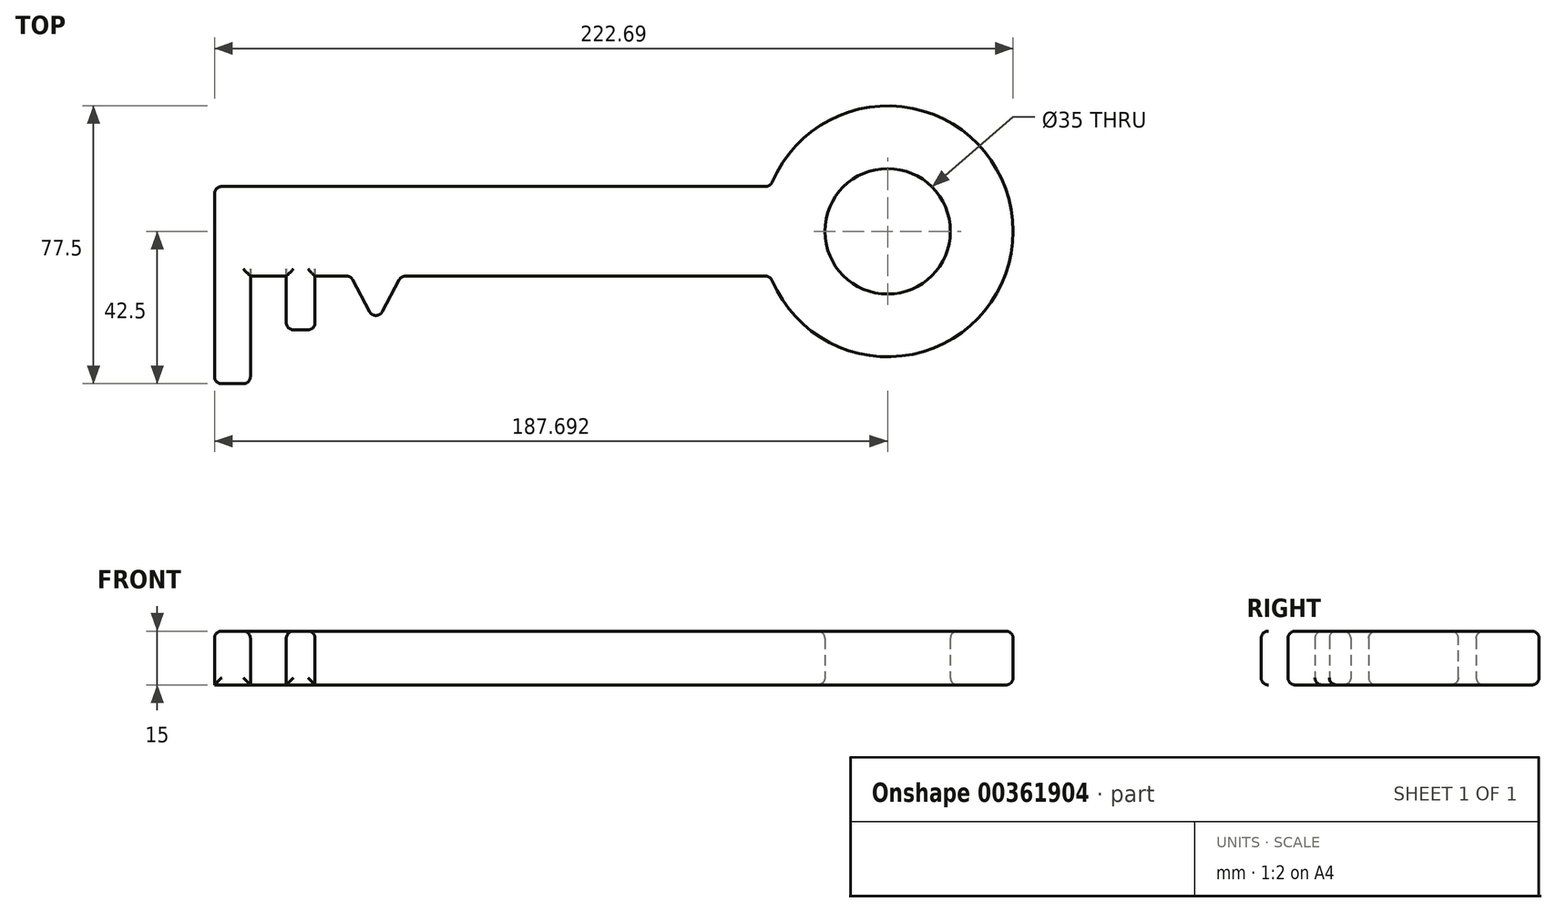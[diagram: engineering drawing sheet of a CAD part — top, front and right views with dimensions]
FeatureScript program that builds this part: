
annotation { "Feature Type Name" : "Feature", "Feature Type Description" : "" }
export const myFeature = defineFeature(function(context is Context, id is Id, definition is map)
    precondition{}
    {
        {
            var Q0;
            Q0=qCreatedBy(makeId("Top.planeOp"),FACE);
            var sketch = newSketch(context, id + "F0", { "sketchPlane" : qUnion([Q0])});
            skLineSegment(sketch, "E0.bottom", {"start": v(0, 0) * mm, "end": v(-155, 0) * mm});
            skLineSegment(sketch, "E0.top", {"start": v(0, 25) * mm, "end": v(-155, 25) * mm});
            skLineSegment(sketch, "E0.left", {"start": v(0, 0) * mm, "end": v(0, 25) * mm});
            skLineSegment(sketch, "E0.right", {"start": v(-155, 0) * mm, "end": v(-155, 25) * mm});
            skLineSegment(sketch, "E1.bottom", {"start": v(-155, 0) * mm, "end": v(-145, 0) * mm});
            skLineSegment(sketch, "E1.top", {"start": v(-155, -30) * mm, "end": v(-145, -30) * mm});
            skLineSegment(sketch, "E1.left", {"start": v(-155, 0) * mm, "end": v(-155, -30) * mm});
            skLineSegment(sketch, "E1.right", {"start": v(-145, 0) * mm, "end": v(-145, -30) * mm});
            skLineSegment(sketch, "E2.bottom", {"start": v(-135, 0) * mm, "end": v(-127, 0) * mm});
            skLineSegment(sketch, "E2.top", {"start": v(-135, -15) * mm, "end": v(-127, -15) * mm});
            skLineSegment(sketch, "E2.left", {"start": v(-135, 0) * mm, "end": v(-135, -15) * mm});
            skLineSegment(sketch, "E2.right", {"start": v(-127, 0) * mm, "end": v(-127, -15) * mm});
            skLineSegment(sketch, "E3", {"start": v(-117, 0) * mm, "end": v(-110, -13.26) * mm});
            skLineSegment(sketch, "E4", {"start": v(-110, 0) * mm, "end": v(-110, -13.26) * mm});
            skLineSegment(sketch, "E5", {"start": v(-110, -13.26) * mm, "end": v(-102.98, 0) * mm});
            skArc(sketch, "E6", {"start": v(0, 0) * mm, "mid": v(67.7, 12.5) * mm, "end": v(0, 25) * mm});
            skCircle(sketch, "E7", {"center": v(32.7, 12.5) * mm, "radius": 17.5 * mm});
            skLineSegment(sketch, "E8", {"start": v(32.7, 12.5) * mm, "end": v(-155, 12.5) * mm, "construction": true});
            skSolve(sketch);
        }
        {
            var Q0;
            Q0 = qSketchRegion(id + "F0", true);
            extrude(context, id + "F1", {"entities" : qUnion([Q0]), "depth" : 15 * mm});
        }
        {
            var Q0;
            Q0=makeQuery(id+"F1.opExtrude","CAP_EDGE",EDGE,{"disambiguationData":[OSD([sQuery(id+"F0.wireOp",EDGE,"E0.top")])],"isStart":false});
            var Q1;
            {var subQ0=sQuery(id+"F0.wireOp",EDGE,"E0.bottom");Q1=makeQuery(id+"F1.opExtrude","CAP_EDGE",EDGE,{"disambiguationData":[OSD([subQ0]),TDD([makeQuery(id+"F0.imprint","IMPRINT",EDGE,{"disambiguationData":[TD([[makeQuery(id+"F0.imprint","INTERSECT",VERTEX,{"derivedFrom":[subQ0,sQuery(id+"F0.wireOp",EDGE,"E5")]}),1.0]])],"derivedFrom":subQ0})])],"isStart":true});}
            var Q2;
            Q2=makeQuery(id+"F1.opExtrude","CAP_EDGE",EDGE,{"disambiguationData":[OSD([sQuery(id+"F0.wireOp",EDGE,"E0.right"),sQuery(id+"F0.wireOp",EDGE,"E1.left")])],"isStart":false});
            var Q3;
            Q3=makeQuery(id+"F1.opExtrude","CAP_EDGE",EDGE,{"disambiguationData":[OSD([sQuery(id+"F0.wireOp",EDGE,"E1.top")])],"isStart":false});
            var Q4;
            Q4=makeQuery(id+"F1.opExtrude","CAP_EDGE",EDGE,{"disambiguationData":[OSD([sQuery(id+"F0.wireOp",EDGE,"E1.right")])],"isStart":false});
            var Q5;
            {var subQ0=sQuery(id+"F0.wireOp",EDGE,"E0.bottom");Q5=makeQuery(id+"F1.opExtrude","CAP_EDGE",EDGE,{"disambiguationData":[OSD([subQ0]),TDD([makeQuery(id+"F0.imprint","IMPRINT",EDGE,{"disambiguationData":[TD([[makeQuery(id+"F0.imprint","INTERSECT",VERTEX,{"derivedFrom":[subQ0,sQuery(id+"F0.wireOp",EDGE,"E1.bottom"),sQuery(id+"F0.wireOp",EDGE,"E1.right")]}),1.0]])],"derivedFrom":subQ0})])],"isStart":false});}
            var Q6;
            Q6=makeQuery(id+"F1.opExtrude","CAP_EDGE",EDGE,{"disambiguationData":[OSD([sQuery(id+"F0.wireOp",EDGE,"E2.left")])],"isStart":false});
            var Q7;
            Q7=makeQuery(id+"F1.opExtrude","CAP_EDGE",EDGE,{"disambiguationData":[OSD([sQuery(id+"F0.wireOp",EDGE,"E2.top")])],"isStart":false});
            var Q8;
            {var subQ0=sQuery(id+"F0.wireOp",EDGE,"E0.bottom");Q8=makeQuery(id+"F1.opExtrude","CAP_EDGE",EDGE,{"disambiguationData":[OSD([subQ0]),TDD([makeQuery(id+"F0.imprint","IMPRINT",EDGE,{"disambiguationData":[TD([[makeQuery(id+"F0.imprint","INTERSECT",VERTEX,{"derivedFrom":[subQ0,sQuery(id+"F0.wireOp",EDGE,"E3")]}),-1.0]])],"derivedFrom":subQ0})])],"isStart":true});}
            var Q9;
            Q9=makeQuery(id+"F1.opExtrude","CAP_EDGE",EDGE,{"disambiguationData":[OSD([sQuery(id+"F0.wireOp",EDGE,"E3")])],"isStart":false});
            var Q10;
            Q10=makeQuery(id+"F1.opExtrude","CAP_EDGE",EDGE,{"disambiguationData":[OSD([sQuery(id+"F0.wireOp",EDGE,"E5")])],"isStart":true});
            var Q11;
            Q11=makeQuery(id+"F1.opExtrude","CAP_EDGE",EDGE,{"disambiguationData":[OSD([sQuery(id+"F0.wireOp",EDGE,"E6")])],"isStart":false});
            var Q12;
            Q12=makeQuery(id+"F1.opExtrude","CAP_EDGE",EDGE,{"disambiguationData":[OSD([sQuery(id+"F0.wireOp",EDGE,"E7")])],"isStart":true});
            var Q13;
            Q13=makeQuery(id+"F1.opExtrude","CAP_EDGE",EDGE,{"disambiguationData":[OSD([sQuery(id+"F0.wireOp",EDGE,"E0.top")])],"isStart":true});
            var Q14;
            Q14=makeQuery(id+"F1.opExtrude","SWEPT_FACE",FACE,{"disambiguationData":[OSD([sQuery(id+"F0.wireOp",EDGE,"E6")])]});
            var Q15;
            Q15=makeQuery(id+"F1.opExtrude","CAP_EDGE",EDGE,{"disambiguationData":[OSD([sQuery(id+"F0.wireOp",EDGE,"E6")])],"isStart":true});
            var Q16;
            {var subQ0=sQuery(id+"F0.wireOp",EDGE,"E0.bottom");Q16=makeQuery(id+"F1.opExtrude","CAP_EDGE",EDGE,{"disambiguationData":[OSD([subQ0]),TDD([makeQuery(id+"F0.imprint","IMPRINT",EDGE,{"disambiguationData":[TD([[makeQuery(id+"F0.imprint","INTERSECT",VERTEX,{"derivedFrom":[subQ0,sQuery(id+"F0.wireOp",EDGE,"E5")]}),1.0]])],"derivedFrom":subQ0})])],"isStart":false});}
            var Q17;
            Q17=makeQuery(id+"F1.opExtrude","SWEPT_EDGE",EDGE,{"disambiguationData":[OSD([sQuery(id+"F0.wireOp",EDGE,"E0.bottom"),sQuery(id+"F0.wireOp",EDGE,"E5")])]});
            var Q18;
            Q18=makeQuery(id+"F1.opExtrude","SWEPT_EDGE",EDGE,{"disambiguationData":[OSD([sQuery(id+"F0.wireOp",EDGE,"E3"),sQuery(id+"F0.wireOp",EDGE,"E4"),sQuery(id+"F0.wireOp",EDGE,"E5")])]});
            var Q19;
            Q19=makeQuery(id+"F1.opExtrude","CAP_EDGE",EDGE,{"disambiguationData":[OSD([sQuery(id+"F0.wireOp",EDGE,"E5")])],"isStart":false});
            var Q20;
            Q20=makeQuery(id+"F1.opExtrude","CAP_EDGE",EDGE,{"disambiguationData":[OSD([sQuery(id+"F0.wireOp",EDGE,"E3")])],"isStart":true});
            var Q21;
            Q21=makeQuery(id+"F1.opExtrude","SWEPT_EDGE",EDGE,{"disambiguationData":[OSD([sQuery(id+"F0.wireOp",EDGE,"E0.bottom"),sQuery(id+"F0.wireOp",EDGE,"E3")])]});
            var Q22;
            {var subQ0=sQuery(id+"F0.wireOp",EDGE,"E0.bottom");Q22=makeQuery(id+"F1.opExtrude","CAP_EDGE",EDGE,{"disambiguationData":[OSD([subQ0]),TDD([makeQuery(id+"F0.imprint","IMPRINT",EDGE,{"disambiguationData":[TD([[makeQuery(id+"F0.imprint","INTERSECT",VERTEX,{"derivedFrom":[subQ0,sQuery(id+"F0.wireOp",EDGE,"E3")]}),-1.0]])],"derivedFrom":subQ0})])],"isStart":false});}
            var Q23;
            Q23=makeQuery(id+"F1.opExtrude","CAP_EDGE",EDGE,{"disambiguationData":[OSD([sQuery(id+"F0.wireOp",EDGE,"E2.right")])],"isStart":false});
            var Q24;
            Q24=makeQuery(id+"F1.opExtrude","CAP_EDGE",EDGE,{"disambiguationData":[OSD([sQuery(id+"F0.wireOp",EDGE,"E2.top")])],"isStart":true});
            var Q25;
            {var subQ0=sQuery(id+"F0.wireOp",EDGE,"E0.bottom");Q25=makeQuery(id+"F1.opExtrude","CAP_EDGE",EDGE,{"disambiguationData":[OSD([subQ0]),TDD([makeQuery(id+"F0.imprint","IMPRINT",EDGE,{"disambiguationData":[TD([[makeQuery(id+"F0.imprint","INTERSECT",VERTEX,{"derivedFrom":[subQ0,sQuery(id+"F0.wireOp",EDGE,"E1.bottom"),sQuery(id+"F0.wireOp",EDGE,"E1.right")]}),1.0]])],"derivedFrom":subQ0})])],"isStart":true});}
            var Q26;
            Q26=makeQuery(id+"F1.opExtrude","SWEPT_EDGE",EDGE,{"disambiguationData":[OSD([sQuery(id+"F0.wireOp",EDGE,"E2.top"),sQuery(id+"F0.wireOp",EDGE,"E2.left")])]});
            var Q27;
            Q27=makeQuery(id+"F1.opExtrude","SWEPT_EDGE",EDGE,{"disambiguationData":[OSD([sQuery(id+"F0.wireOp",EDGE,"E1.top"),sQuery(id+"F0.wireOp",EDGE,"E1.right")])]});
            var Q28;
            Q28=makeQuery(id+"F1.opExtrude","CAP_EDGE",EDGE,{"disambiguationData":[OSD([sQuery(id+"F0.wireOp",EDGE,"E1.top")])],"isStart":true});
            var Q29;
            Q29=makeQuery(id+"F1.opExtrude","SWEPT_EDGE",EDGE,{"disambiguationData":[OSD([sQuery(id+"F0.wireOp",EDGE,"E1.top"),sQuery(id+"F0.wireOp",EDGE,"E1.left")])]});
            var Q30;
            Q30=makeQuery(id+"F1.opExtrude","SWEPT_EDGE",EDGE,{"disambiguationData":[OSD([sQuery(id+"F0.wireOp",EDGE,"E2.top"),sQuery(id+"F0.wireOp",EDGE,"E2.right")])]});
            var Q31;
            Q31=makeQuery(id+"F1.opExtrude","CAP_EDGE",EDGE,{"disambiguationData":[OSD([sQuery(id+"F0.wireOp",EDGE,"E7")])],"isStart":false});
            var Q32;
            Q32=makeQuery(id+"F1.opExtrude","SWEPT_FACE",FACE,{"disambiguationData":[OSD([sQuery(id+"F0.wireOp",EDGE,"E0.top")])]});
            var Q33;
            Q33=makeQuery(id+"F1.opExtrude","SWEPT_EDGE",EDGE,{"disambiguationData":[OSD([sQuery(id+"F0.wireOp",EDGE,"E0.top"),sQuery(id+"F0.wireOp",EDGE,"E0.right")])]});
            fillet(context, id + "F2", {"entities" : qUnion([Q0, Q1, Q2, Q3, Q4, Q5, Q6, Q7, Q8, Q9, Q10, Q11, Q12, Q13, Q14, Q15, Q16, Q17, Q18, Q19, Q20, Q21, Q22, Q23, Q24, Q25, Q26, Q27, Q28, Q29, Q30, Q31, Q32, Q33]), "radius" : 2 * mm, "tangentPropagation" : true, "allowEdgeOverflow" : false});
        }
    });
